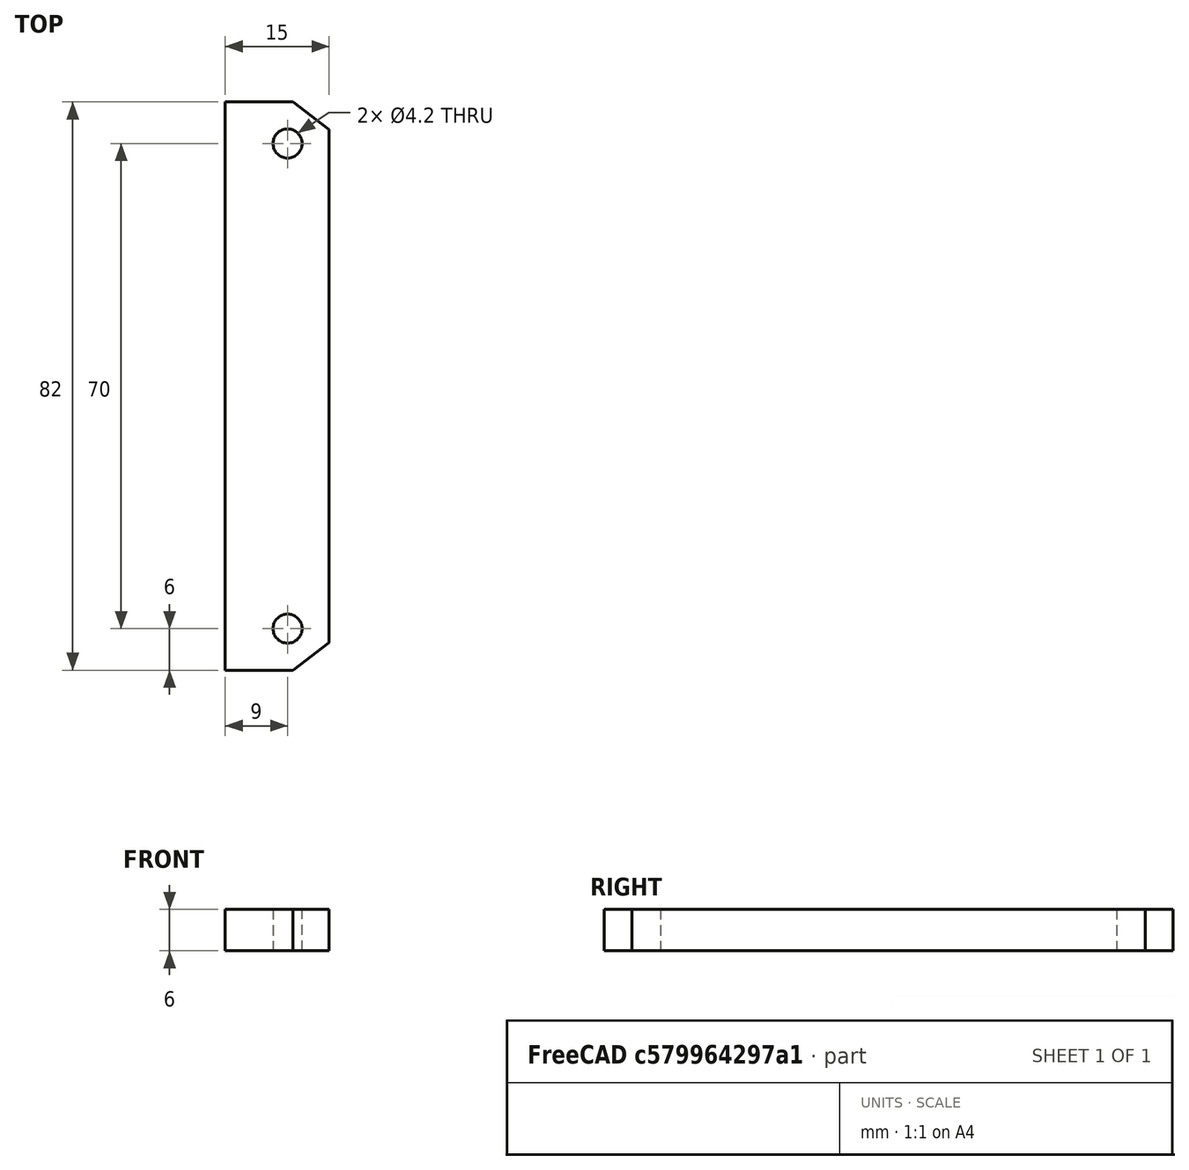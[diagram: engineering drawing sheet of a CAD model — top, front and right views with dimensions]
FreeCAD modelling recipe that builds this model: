
FCSTD DOCUMENT  (FreeCAD 0.16R6712 (Git))
Label: Enclosure_supports_01
License: All rights reserved
LicenseURL: http://en.wikipedia.org/wiki/All_rights_reserved
objects: Sketcher::SketchObject×2, PartDesign::Pad×1
note: 4 computed .brp shape members not serialized (recipe doc carries the construction recipe); baked Part::Feature solids carry a one-line shape summary decoded from their .brp

FEATURE [Sketcher::SketchObject] Sketch
  sketch-geometry (8):
    g0: LineSegment StartX=0 StartY=82 StartZ=0 EndX=0 EndY=0 EndZ=0
    g1: LineSegment StartX=14.9996 StartY=4 StartZ=0 EndX=14.9996 EndY=78 EndZ=0
    g2: Circle CenterX=9 CenterY=6 CenterZ=0 NormalX=0 NormalY=0 NormalZ=1 Radius=2.1
    g3: Circle CenterX=9 CenterY=76 CenterZ=0 NormalX=0 NormalY=0 NormalZ=1 Radius=2.1
    g4: LineSegment StartX=0 StartY=0 StartZ=0 EndX=9.78741 EndY=0 EndZ=0
    g5: LineSegment StartX=9.78741 StartY=0 StartZ=0 EndX=14.9996 EndY=4 EndZ=0
    g6: LineSegment StartX=0 StartY=82 StartZ=0 EndX=9.78741 EndY=82 EndZ=0
    g7: LineSegment StartX=9.78741 StartY=82 StartZ=0 EndX=14.9996 EndY=78 EndZ=0
  constraints (22):
    c: PointOnObject(g0,g-2)
    c: Vertical(g0)
    c: Vertical(g1)
    c: Radius(g2) = 2.1
    c: Equal(g2,g3)
    c: Distance(g1) = 74
    c: Distance(g0) = 82
    c: Coincident(g-1,g0)
    c: Distance(g3,g2) = 70
    c: Horizontal(g4)
    c: Coincident(g4,g5)
    c: Coincident(g5,g1)
    c: Coincident(g4,g-1)
    c: Coincident(g0,g6)
    c: Horizontal(g6)
    c: Coincident(g6,g7)
    c: Coincident(g7,g1)
    c: Equal(g6,g4)
    c: Equal(g7,g5)
    c: Distance(g3,g0) = 9
    c: Distance(g2,g0) = 9
    c: Distance(g3,g6) = 6
FEATURE [PartDesign::Pad] Pad
  Length = 6
  Length2 = 100
  Sketch = -> Sketch
  Type = 0
FEATURE [Sketcher::SketchObject] Sketch001
  Placement = pos=(14.9996,0,0) rot=(0.57735,0.57735,0.57735;2.0944rad)
  Support = -> Pad [Face4]
  sketch-geometry (4):
    g0: LineSegment StartX=20 StartY=4.4417 StartZ=0 EndX=70 EndY=4.4417 EndZ=0
    g1: LineSegment StartX=70 StartY=4.4417 StartZ=0 EndX=70 EndY=0.9417 EndZ=0
    g2: LineSegment StartX=70 StartY=0.9417 StartZ=0 EndX=20 EndY=0.9417 EndZ=0
    g3: LineSegment StartX=20 StartY=0.9417 StartZ=0 EndX=20 EndY=4.4417 EndZ=0
  constraints (11):
    c: Coincident(g0,g1)
    c: Coincident(g1,g2)
    c: Coincident(g2,g3)
    c: Coincident(g3,g0)
    c: Horizontal(g0)
    c: Horizontal(g2)
    c: Vertical(g1)
    c: Vertical(g3)
    c: Distance(g2) = 50
    c: Distance(g3) = 3.5
    c: DistanceX(g-2,g2) = 20
